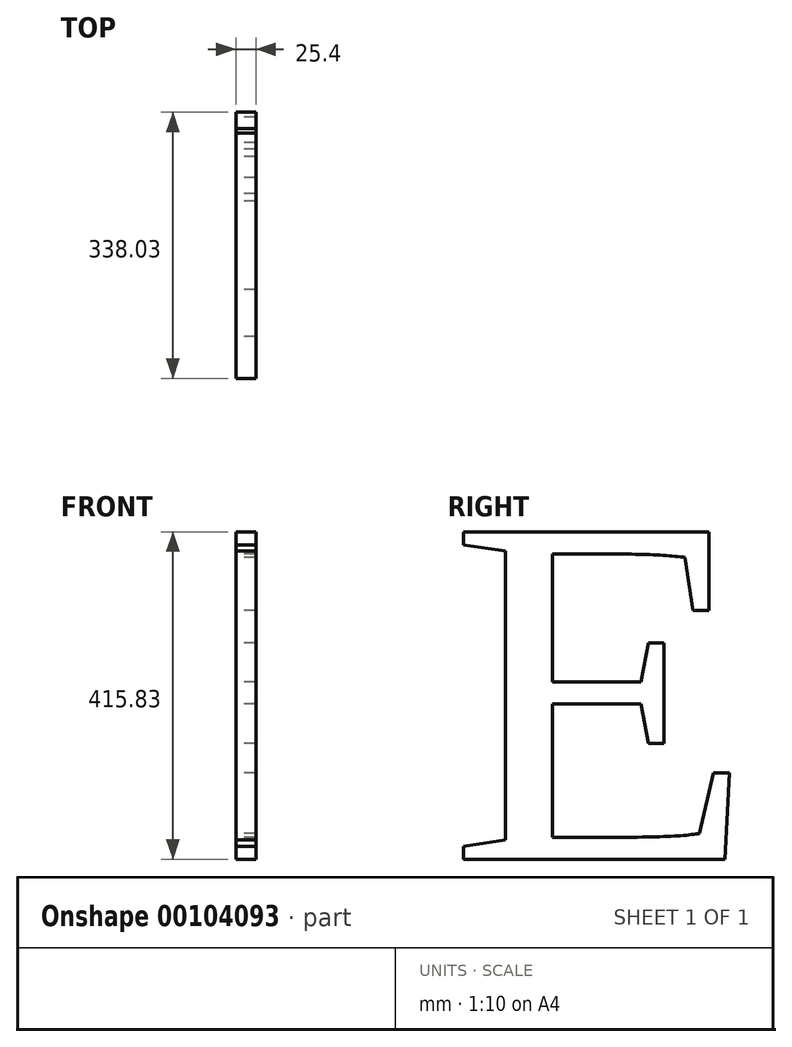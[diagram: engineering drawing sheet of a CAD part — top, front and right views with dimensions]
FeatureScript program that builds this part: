
annotation { "Feature Type Name" : "Feature", "Feature Type Description" : "" }
export const myFeature = defineFeature(function(context is Context, id is Id, definition is map)
    precondition{}
    {
        {
            var Q0;
            Q0=qCreatedBy(makeId("Right.planeOp"),FACE);
            var sketch = newSketch(context, id + "F0", { "sketchPlane" : qUnion([Q0])});
            skText(sketch, "E0", { "text": "E", "fontName": "Tinos-Regular.ttf"});
            const initialGuessF0  = {"E0": [-0.50817, 0, 1, 0, 0.4572]};
            skSetInitialGuess(sketch, initialGuessF0);
            skSolve(sketch);
        }
        {
            var Q0;
            Q0 = qSketchRegion(id + "F0", true);
            extrude(context, id + "F1", {"entities" : qUnion([Q0]), "depth" : 25.4 * mm});
        }
    });
